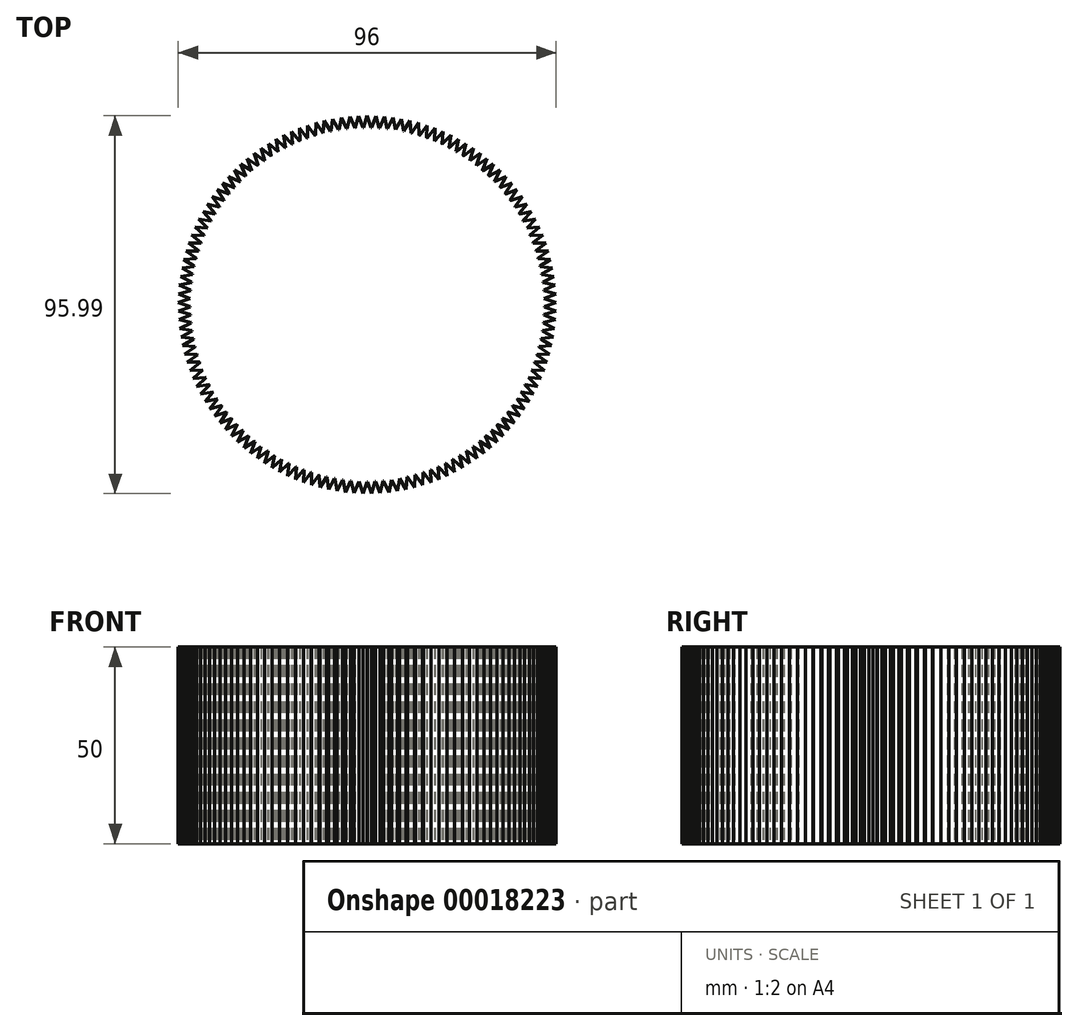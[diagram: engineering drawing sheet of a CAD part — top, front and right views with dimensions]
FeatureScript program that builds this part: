
annotation { "Feature Type Name" : "Feature", "Feature Type Description" : "" }
export const myFeature = defineFeature(function(context is Context, id is Id, definition is map)
    precondition{}
    {
        {
            var Q0;
            Q0=qCreatedBy(makeId("Top.planeOp"),FACE);
            var sketch = newSketch(context, id + "F0", { "sketchPlane" : qUnion([Q0])});
            skCircle(sketch, "E0", {"center": v(0, 0) * mm, "radius": 46.5 * mm, "construction": true});
            skLineSegment(sketch, "E1", {"start": v(0, 0) * mm, "end": v(0, 46.5) * mm, "construction": true});
            skCircle(sketch, "E2.0", {"center": v(0, 0) * mm, "radius": 48 * mm, "construction": true});
            skCircle(sketch, "E3.0", {"center": v(0, 0) * mm, "radius": 45 * mm});
            skLineSegment(sketch, "E4", {"start": v(-0.98, 44.99) * mm, "end": v(0, 48) * mm});
            skLineSegment(sketch, "E5", {"start": v(0, 48) * mm, "end": v(0.98, 44.99) * mm});
            skLineSegment(sketch, "E6.1.0", {"start": v(-2.2, 47.95) * mm, "end": v(-1.09, 44.99) * mm});
            skLineSegment(sketch, "E6.1.1", {"start": v(-3.04, 44.9) * mm, "end": v(-2.2, 47.95) * mm});
            skLineSegment(sketch, "E6.2.0", {"start": v(-4.4, 47.8) * mm, "end": v(-3.15, 44.89) * mm});
            skLineSegment(sketch, "E6.2.1", {"start": v(-5.1, 44.71) * mm, "end": v(-4.4, 47.8) * mm});
            skLineSegment(sketch, "E6.3.0", {"start": v(-6.58, 47.55) * mm, "end": v(-5.2, 44.7) * mm});
            skLineSegment(sketch, "E6.3.1", {"start": v(-7.14, 44.43) * mm, "end": v(-6.58, 47.55) * mm});
            skLineSegment(sketch, "E6.4.0", {"start": v(-8.76, 47.2) * mm, "end": v(-7.25, 44.41) * mm});
            skLineSegment(sketch, "E6.4.1", {"start": v(-9.17, 44.06) * mm, "end": v(-8.76, 47.2) * mm});
            skLineSegment(sketch, "E6.5.0", {"start": v(-10.91, 46.74) * mm, "end": v(-9.27, 44.03) * mm});
            skLineSegment(sketch, "E6.5.1", {"start": v(-11.18, 43.59) * mm, "end": v(-10.91, 46.74) * mm});
            skLineSegment(sketch, "E6.6.0", {"start": v(-13.04, 46.2) * mm, "end": v(-11.28, 43.56) * mm});
            skLineSegment(sketch, "E6.6.1", {"start": v(-13.17, 43.03) * mm, "end": v(-13.04, 46.2) * mm});
            skLineSegment(sketch, "E6.7.0", {"start": v(-15.15, 45.55) * mm, "end": v(-13.27, 43) * mm});
            skLineSegment(sketch, "E6.7.1", {"start": v(-15.12, 42.38) * mm, "end": v(-15.15, 45.55) * mm});
            skLineSegment(sketch, "E6.8.0", {"start": v(-17.22, 44.8) * mm, "end": v(-15.23, 42.35) * mm});
            skLineSegment(sketch, "E6.8.1", {"start": v(-17.05, 41.64) * mm, "end": v(-17.22, 44.8) * mm});
            skLineSegment(sketch, "E6.9.0", {"start": v(-19.25, 43.97) * mm, "end": v(-17.15, 41.6) * mm});
            skLineSegment(sketch, "E6.9.1", {"start": v(-18.94, 40.82) * mm, "end": v(-19.25, 43.97) * mm});
            skLineSegment(sketch, "E6.10.0", {"start": v(-21.25, 43.04) * mm, "end": v(-19.04, 40.77) * mm});
            skLineSegment(sketch, "E6.10.1", {"start": v(-20.8, 39.9) * mm, "end": v(-21.25, 43.04) * mm});
            skLineSegment(sketch, "E6.11.0", {"start": v(-23.2, 42.02) * mm, "end": v(-20.89, 39.86) * mm});
            skLineSegment(sketch, "E6.11.1", {"start": v(-22.6, 38.91) * mm, "end": v(-23.2, 42.02) * mm});
            skLineSegment(sketch, "E6.12.0", {"start": v(-25.1, 40.91) * mm, "end": v(-22.7, 38.86) * mm});
            skLineSegment(sketch, "E6.12.1", {"start": v(-24.36, 37.83) * mm, "end": v(-25.1, 40.91) * mm});
            skLineSegment(sketch, "E6.13.0", {"start": v(-26.95, 39.72) * mm, "end": v(-24.45, 37.78) * mm});
            skLineSegment(sketch, "E6.13.1", {"start": v(-26.07, 36.68) * mm, "end": v(-26.95, 39.72) * mm});
            skLineSegment(sketch, "E6.14.0", {"start": v(-28.75, 38.44) * mm, "end": v(-26.16, 36.62) * mm});
            skLineSegment(sketch, "E6.14.1", {"start": v(-27.73, 35.44) * mm, "end": v(-28.75, 38.44) * mm});
            skLineSegment(sketch, "E6.15.0", {"start": v(-30.48, 37.08) * mm, "end": v(-27.81, 35.38) * mm});
            skLineSegment(sketch, "E6.15.1", {"start": v(-29.32, 34.14) * mm, "end": v(-30.48, 37.08) * mm});
            skLineSegment(sketch, "E6.16.0", {"start": v(-32.15, 35.65) * mm, "end": v(-29.4, 34.07) * mm});
            skLineSegment(sketch, "E6.16.1", {"start": v(-30.86, 32.76) * mm, "end": v(-32.15, 35.65) * mm});
            skLineSegment(sketch, "E6.17.0", {"start": v(-33.75, 34.14) * mm, "end": v(-30.93, 32.68) * mm});
            skLineSegment(sketch, "E6.17.1", {"start": v(-32.33, 31.3) * mm, "end": v(-33.75, 34.14) * mm});
            skLineSegment(sketch, "E6.18.0", {"start": v(-35.28, 32.55) * mm, "end": v(-32.4, 31.23) * mm});
            skLineSegment(sketch, "E6.18.1", {"start": v(-33.73, 29.8) * mm, "end": v(-35.28, 32.55) * mm});
            skLineSegment(sketch, "E6.19.0", {"start": v(-36.73, 30.9) * mm, "end": v(-33.8, 29.71) * mm});
            skLineSegment(sketch, "E6.19.1", {"start": v(-35.06, 28.21) * mm, "end": v(-36.73, 30.9) * mm});
            skLineSegment(sketch, "E6.20.0", {"start": v(-38.1, 29.18) * mm, "end": v(-35.12, 28.13) * mm});
            skLineSegment(sketch, "E6.20.1", {"start": v(-36.31, 26.58) * mm, "end": v(-38.1, 29.18) * mm});
            skLineSegment(sketch, "E6.21.0", {"start": v(-39.4, 27.4) * mm, "end": v(-36.38, 26.5) * mm});
            skLineSegment(sketch, "E6.21.1", {"start": v(-37.5, 24.88) * mm, "end": v(-39.4, 27.4) * mm});
            skLineSegment(sketch, "E6.22.0", {"start": v(-40.62, 25.57) * mm, "end": v(-37.55, 24.8) * mm});
            skLineSegment(sketch, "E6.22.1", {"start": v(-38.6, 23.14) * mm, "end": v(-40.62, 25.57) * mm});
            skLineSegment(sketch, "E6.23.0", {"start": v(-41.75, 23.68) * mm, "end": v(-38.65, 23.05) * mm});
            skLineSegment(sketch, "E6.23.1", {"start": v(-39.62, 21.35) * mm, "end": v(-41.75, 23.68) * mm});
            skLineSegment(sketch, "E6.24.0", {"start": v(-42.8, 21.74) * mm, "end": v(-39.67, 21.25) * mm});
            skLineSegment(sketch, "E6.24.1", {"start": v(-40.55, 19.5) * mm, "end": v(-42.8, 21.74) * mm});
            skLineSegment(sketch, "E6.25.0", {"start": v(-43.75, 19.76) * mm, "end": v(-40.6, 19.4) * mm});
            skLineSegment(sketch, "E6.25.1", {"start": v(-41.4, 17.63) * mm, "end": v(-43.75, 19.76) * mm});
            skLineSegment(sketch, "E6.26.0", {"start": v(-44.6, 17.73) * mm, "end": v(-41.45, 17.53) * mm});
            skLineSegment(sketch, "E6.26.1", {"start": v(-42.17, 15.71) * mm, "end": v(-44.6, 17.73) * mm});
            skLineSegment(sketch, "E6.27.0", {"start": v(-45.37, 15.67) * mm, "end": v(-42.2, 15.6) * mm});
            skLineSegment(sketch, "E6.27.1", {"start": v(-42.84, 13.76) * mm, "end": v(-45.37, 15.67) * mm});
            skLineSegment(sketch, "E6.28.0", {"start": v(-46.04, 13.57) * mm, "end": v(-42.88, 13.66) * mm});
            skLineSegment(sketch, "E6.28.1", {"start": v(-43.43, 11.78) * mm, "end": v(-46.04, 13.57) * mm});
            skLineSegment(sketch, "E6.29.0", {"start": v(-46.62, 11.45) * mm, "end": v(-43.46, 11.68) * mm});
            skLineSegment(sketch, "E6.29.1", {"start": v(-43.92, 9.78) * mm, "end": v(-46.62, 11.45) * mm});
            skLineSegment(sketch, "E6.30.0", {"start": v(-47.1, 9.3) * mm, "end": v(-43.95, 9.67) * mm});
            skLineSegment(sketch, "E6.30.1", {"start": v(-44.33, 7.75) * mm, "end": v(-47.1, 9.3) * mm});
            skLineSegment(sketch, "E6.31.0", {"start": v(-47.47, 7.13) * mm, "end": v(-44.35, 7.65) * mm});
            skLineSegment(sketch, "E6.31.1", {"start": v(-44.64, 5.71) * mm, "end": v(-47.47, 7.13) * mm});
            skLineSegment(sketch, "E6.32.0", {"start": v(-47.74, 4.94) * mm, "end": v(-44.65, 5.6) * mm});
            skLineSegment(sketch, "E6.32.1", {"start": v(-44.85, 3.66) * mm, "end": v(-47.74, 4.94) * mm});
            skLineSegment(sketch, "E6.33.0", {"start": v(-47.92, 2.75) * mm, "end": v(-44.86, 3.55) * mm});
            skLineSegment(sketch, "E6.33.1", {"start": v(-44.97, 1.6) * mm, "end": v(-47.92, 2.75) * mm});
            skLineSegment(sketch, "E6.34.0", {"start": v(-48, 0.55) * mm, "end": v(-44.98, 1.5) * mm});
            skLineSegment(sketch, "E6.34.1", {"start": v(-45, -0.46) * mm, "end": v(-48, 0.55) * mm});
            skLineSegment(sketch, "E6.35.0", {"start": v(-47.97, -1.65) * mm, "end": v(-45, -0.57) * mm});
            skLineSegment(sketch, "E6.35.1", {"start": v(-44.93, -2.52) * mm, "end": v(-47.97, -1.65) * mm});
            skLineSegment(sketch, "E6.36.0", {"start": v(-47.85, -3.85) * mm, "end": v(-44.92, -2.63) * mm});
            skLineSegment(sketch, "E6.36.1", {"start": v(-44.77, -4.58) * mm, "end": v(-47.85, -3.85) * mm});
            skLineSegment(sketch, "E6.37.0", {"start": v(-47.62, -6.04) * mm, "end": v(-44.76, -4.69) * mm});
            skLineSegment(sketch, "E6.37.1", {"start": v(-44.5, -6.63) * mm, "end": v(-47.62, -6.04) * mm});
            skLineSegment(sketch, "E6.38.0", {"start": v(-47.3, -8.21) * mm, "end": v(-44.5, -6.74) * mm});
            skLineSegment(sketch, "E6.38.1", {"start": v(-44.16, -8.66) * mm, "end": v(-47.3, -8.21) * mm});
            skLineSegment(sketch, "E6.39.0", {"start": v(-46.87, -10.37) * mm, "end": v(-44.14, -8.77) * mm});
            skLineSegment(sketch, "E6.39.1", {"start": v(-43.71, -10.68) * mm, "end": v(-46.87, -10.37) * mm});
            skLineSegment(sketch, "E6.40.0", {"start": v(-46.34, -12.51) * mm, "end": v(-43.69, -10.78) * mm});
            skLineSegment(sketch, "E6.40.1", {"start": v(-43.18, -12.67) * mm, "end": v(-46.34, -12.51) * mm});
            skLineSegment(sketch, "E6.41.0", {"start": v(-45.72, -14.62) * mm, "end": v(-43.15, -12.77) * mm});
            skLineSegment(sketch, "E6.41.1", {"start": v(-42.55, -14.64) * mm, "end": v(-45.72, -14.62) * mm});
            skLineSegment(sketch, "E6.42.0", {"start": v(-45, -16.7) * mm, "end": v(-42.52, -14.74) * mm});
            skLineSegment(sketch, "E6.42.1", {"start": v(-41.84, -16.57) * mm, "end": v(-45, -16.7) * mm});
            skLineSegment(sketch, "E6.43.0", {"start": v(-44.19, -18.75) * mm, "end": v(-41.8, -16.67) * mm});
            skLineSegment(sketch, "E6.43.1", {"start": v(-41.03, -18.47) * mm, "end": v(-44.19, -18.75) * mm});
            skLineSegment(sketch, "E6.44.0", {"start": v(-43.28, -20.76) * mm, "end": v(-40.99, -18.57) * mm});
            skLineSegment(sketch, "E6.44.1", {"start": v(-40.14, -20.34) * mm, "end": v(-43.28, -20.76) * mm});
            skLineSegment(sketch, "E6.45.0", {"start": v(-42.28, -22.72) * mm, "end": v(-40.1, -20.43) * mm});
            skLineSegment(sketch, "E6.45.1", {"start": v(-39.17, -22.15) * mm, "end": v(-42.28, -22.72) * mm});
            skLineSegment(sketch, "E6.46.0", {"start": v(-41.2, -24.63) * mm, "end": v(-39.12, -22.25) * mm});
            skLineSegment(sketch, "E6.46.1", {"start": v(-38.11, -23.93) * mm, "end": v(-41.2, -24.63) * mm});
            skLineSegment(sketch, "E6.47.0", {"start": v(-40.02, -26.5) * mm, "end": v(-38.05, -24.02) * mm});
            skLineSegment(sketch, "E6.47.1", {"start": v(-36.97, -25.65) * mm, "end": v(-40.02, -26.5) * mm});
            skLineSegment(sketch, "E6.48.0", {"start": v(-38.77, -28.3) * mm, "end": v(-36.91, -25.74) * mm});
            skLineSegment(sketch, "E6.48.1", {"start": v(-35.76, -27.32) * mm, "end": v(-38.77, -28.3) * mm});
            skLineSegment(sketch, "E7.2.49.0", {"start": v(-37.43, -30.05) * mm, "end": v(-35.7, -27.4) * mm});
            skLineSegment(sketch, "E7.3.49.0", {"start": v(-34.47, -28.93) * mm, "end": v(-37.43, -30.05) * mm});
            skLineSegment(sketch, "E7.2.50.0", {"start": v(-36.01, -31.73) * mm, "end": v(-34.4, -29.01) * mm});
            skLineSegment(sketch, "E7.3.50.0", {"start": v(-33.1, -30.48) * mm, "end": v(-36.01, -31.73) * mm});
            skLineSegment(sketch, "E7.2.51.0", {"start": v(-34.52, -33.35) * mm, "end": v(-33.03, -30.56) * mm});
            skLineSegment(sketch, "E7.3.51.0", {"start": v(-31.67, -31.96) * mm, "end": v(-34.52, -33.35) * mm});
            skLineSegment(sketch, "E7.2.52.0", {"start": v(-32.95, -34.9) * mm, "end": v(-31.6, -32.04) * mm});
            skLineSegment(sketch, "E7.3.52.0", {"start": v(-30.18, -33.38) * mm, "end": v(-32.95, -34.9) * mm});
            skLineSegment(sketch, "E7.2.53.0", {"start": v(-31.32, -36.37) * mm, "end": v(-30.1, -33.45) * mm});
            skLineSegment(sketch, "E7.3.53.0", {"start": v(-28.61, -34.73) * mm, "end": v(-31.32, -36.37) * mm});
            skLineSegment(sketch, "E7.2.54.0", {"start": v(-29.62, -37.77) * mm, "end": v(-28.53, -34.8) * mm});
            skLineSegment(sketch, "E7.3.54.0", {"start": v(-27, -36) * mm, "end": v(-29.62, -37.77) * mm});
            skLineSegment(sketch, "E7.2.55.0", {"start": v(-27.86, -39.09) * mm, "end": v(-26.9, -36.07) * mm});
            skLineSegment(sketch, "E7.3.55.0", {"start": v(-25.31, -37.2) * mm, "end": v(-27.86, -39.09) * mm});
            skLineSegment(sketch, "E7.2.56.0", {"start": v(-26.03, -40.33) * mm, "end": v(-25.22, -37.27) * mm});
            skLineSegment(sketch, "E7.3.56.0", {"start": v(-23.58, -38.33) * mm, "end": v(-26.03, -40.33) * mm});
            skLineSegment(sketch, "E7.2.57.0", {"start": v(-24.16, -41.48) * mm, "end": v(-23.49, -38.38) * mm});
            skLineSegment(sketch, "E7.3.57.0", {"start": v(-21.8, -39.37) * mm, "end": v(-24.16, -41.48) * mm});
            skLineSegment(sketch, "E7.2.58.0", {"start": v(-22.23, -42.54) * mm, "end": v(-21.7, -39.42) * mm});
            skLineSegment(sketch, "E7.3.58.0", {"start": v(-19.97, -40.33) * mm, "end": v(-22.23, -42.54) * mm});
            skLineSegment(sketch, "E8.2.59.0", {"start": v(-20.26, -43.52) * mm, "end": v(-19.87, -40.37) * mm});
            skLineSegment(sketch, "E8.3.59.0", {"start": v(-18.1, -41.2) * mm, "end": v(-20.26, -43.52) * mm});
            skLineSegment(sketch, "E9.2.60.0", {"start": v(-18.24, -44.4) * mm, "end": v(-18, -41.24) * mm});
            skLineSegment(sketch, "E9.3.60.0", {"start": v(-16.2, -41.99) * mm, "end": v(-18.24, -44.4) * mm});
            skLineSegment(sketch, "E9.2.61.0", {"start": v(-16.19, -45.19) * mm, "end": v(-16.1, -42.02) * mm});
            skLineSegment(sketch, "E9.3.61.0", {"start": v(-14.25, -42.68) * mm, "end": v(-16.19, -45.19) * mm});
            skLineSegment(sketch, "E10.2.62.0", {"start": v(-14.1, -45.88) * mm, "end": v(-14.15, -42.72) * mm});
            skLineSegment(sketch, "E10.3.62.0", {"start": v(-12.28, -43.3) * mm, "end": v(-14.1, -45.88) * mm});
            skLineSegment(sketch, "E11.2.63.0", {"start": v(-11.98, -46.48) * mm, "end": v(-12.18, -43.32) * mm});
            skLineSegment(sketch, "E11.3.63.0", {"start": v(-10.28, -43.8) * mm, "end": v(-11.98, -46.48) * mm});
            skLineSegment(sketch, "E12.2.64.0", {"start": v(-9.84, -46.98) * mm, "end": v(-10.18, -43.83) * mm});
            skLineSegment(sketch, "E12.3.64.0", {"start": v(-8.26, -44.24) * mm, "end": v(-9.84, -46.98) * mm});
            skLineSegment(sketch, "E13.2.65.0", {"start": v(-7.67, -47.38) * mm, "end": v(-8.16, -44.25) * mm});
            skLineSegment(sketch, "E13.3.65.0", {"start": v(-6.23, -44.57) * mm, "end": v(-7.67, -47.38) * mm});
            skLineSegment(sketch, "E13.2.66.0", {"start": v(-5.5, -47.68) * mm, "end": v(-6.12, -44.58) * mm});
            skLineSegment(sketch, "E13.3.66.0", {"start": v(-4.18, -44.8) * mm, "end": v(-5.5, -47.68) * mm});
            skLineSegment(sketch, "E13.2.67.0", {"start": v(-3.3, -47.89) * mm, "end": v(-4.07, -44.82) * mm});
            skLineSegment(sketch, "E13.3.67.0", {"start": v(-2.12, -44.95) * mm, "end": v(-3.3, -47.89) * mm});
            skLineSegment(sketch, "E13.2.68.0", {"start": v(-1.1, -47.99) * mm, "end": v(-2, -44.96) * mm});
            skLineSegment(sketch, "E13.3.68.0", {"start": v(-0.05, -45) * mm, "end": v(-1.1, -47.99) * mm});
            skLineSegment(sketch, "E13.2.69.0", {"start": v(1.1, -47.99) * mm, "end": v(0.05, -45) * mm});
            skLineSegment(sketch, "E13.3.69.0", {"start": v(2, -44.96) * mm, "end": v(1.1, -47.99) * mm});
            skLineSegment(sketch, "E13.2.70.0", {"start": v(3.3, -47.89) * mm, "end": v(2.12, -44.95) * mm});
            skLineSegment(sketch, "E13.3.70.0", {"start": v(4.07, -44.82) * mm, "end": v(3.3, -47.89) * mm});
            skLineSegment(sketch, "E13.2.71.0", {"start": v(5.5, -47.68) * mm, "end": v(4.18, -44.8) * mm});
            skLineSegment(sketch, "E13.3.71.0", {"start": v(6.12, -44.58) * mm, "end": v(5.5, -47.68) * mm});
            skLineSegment(sketch, "E13.2.72.0", {"start": v(7.67, -47.38) * mm, "end": v(6.23, -44.57) * mm});
            skLineSegment(sketch, "E13.3.72.0", {"start": v(8.16, -44.25) * mm, "end": v(7.67, -47.38) * mm});
            skLineSegment(sketch, "E13.2.73.0", {"start": v(9.84, -46.98) * mm, "end": v(8.26, -44.24) * mm});
            skLineSegment(sketch, "E13.3.73.0", {"start": v(10.18, -43.83) * mm, "end": v(9.84, -46.98) * mm});
            skLineSegment(sketch, "E13.2.74.0", {"start": v(11.98, -46.48) * mm, "end": v(10.28, -43.8) * mm});
            skLineSegment(sketch, "E13.3.74.0", {"start": v(12.18, -43.32) * mm, "end": v(11.98, -46.48) * mm});
            skLineSegment(sketch, "E14.2.75.0", {"start": v(14.1, -45.88) * mm, "end": v(12.28, -43.3) * mm});
            skLineSegment(sketch, "E14.3.75.0", {"start": v(14.15, -42.72) * mm, "end": v(14.1, -45.88) * mm});
            skLineSegment(sketch, "E14.2.76.0", {"start": v(16.19, -45.19) * mm, "end": v(14.25, -42.68) * mm});
            skLineSegment(sketch, "E14.3.76.0", {"start": v(16.1, -42.02) * mm, "end": v(16.19, -45.19) * mm});
            skLineSegment(sketch, "E14.2.77.0", {"start": v(18.24, -44.4) * mm, "end": v(16.2, -41.99) * mm});
            skLineSegment(sketch, "E14.3.77.0", {"start": v(18, -41.24) * mm, "end": v(18.24, -44.4) * mm});
            skLineSegment(sketch, "E14.2.78.0", {"start": v(20.26, -43.52) * mm, "end": v(18.1, -41.2) * mm});
            skLineSegment(sketch, "E14.3.78.0", {"start": v(19.87, -40.37) * mm, "end": v(20.26, -43.52) * mm});
            skLineSegment(sketch, "E14.2.79.0", {"start": v(22.23, -42.54) * mm, "end": v(19.97, -40.33) * mm});
            skLineSegment(sketch, "E14.3.79.0", {"start": v(21.7, -39.42) * mm, "end": v(22.23, -42.54) * mm});
            skLineSegment(sketch, "E15.2.80.0", {"start": v(24.16, -41.48) * mm, "end": v(21.8, -39.37) * mm});
            skLineSegment(sketch, "E15.3.80.0", {"start": v(23.49, -38.38) * mm, "end": v(24.16, -41.48) * mm});
            skLineSegment(sketch, "E16.2.81.0", {"start": v(26.03, -40.33) * mm, "end": v(23.58, -38.33) * mm});
            skLineSegment(sketch, "E16.3.81.0", {"start": v(25.22, -37.27) * mm, "end": v(26.03, -40.33) * mm});
            skLineSegment(sketch, "E16.2.82.0", {"start": v(27.86, -39.09) * mm, "end": v(25.31, -37.2) * mm});
            skLineSegment(sketch, "E16.3.82.0", {"start": v(26.9, -36.07) * mm, "end": v(27.86, -39.09) * mm});
            skLineSegment(sketch, "E16.2.83.0", {"start": v(29.62, -37.77) * mm, "end": v(27, -36) * mm});
            skLineSegment(sketch, "E16.3.83.0", {"start": v(28.53, -34.8) * mm, "end": v(29.62, -37.77) * mm});
            skLineSegment(sketch, "E16.2.84.0", {"start": v(31.32, -36.37) * mm, "end": v(28.61, -34.73) * mm});
            skLineSegment(sketch, "E16.3.84.0", {"start": v(30.1, -33.45) * mm, "end": v(31.32, -36.37) * mm});
            skLineSegment(sketch, "E16.2.85.0", {"start": v(32.95, -34.9) * mm, "end": v(30.18, -33.38) * mm});
            skLineSegment(sketch, "E16.3.85.0", {"start": v(31.6, -32.04) * mm, "end": v(32.95, -34.9) * mm});
            skLineSegment(sketch, "E16.2.86.0", {"start": v(34.52, -33.35) * mm, "end": v(31.67, -31.96) * mm});
            skLineSegment(sketch, "E16.3.86.0", {"start": v(33.03, -30.56) * mm, "end": v(34.52, -33.35) * mm});
            skLineSegment(sketch, "E16.2.87.0", {"start": v(36.01, -31.73) * mm, "end": v(33.1, -30.48) * mm});
            skLineSegment(sketch, "E16.3.87.0", {"start": v(34.4, -29.01) * mm, "end": v(36.01, -31.73) * mm});
            skLineSegment(sketch, "E16.2.88.0", {"start": v(37.43, -30.05) * mm, "end": v(34.47, -28.93) * mm});
            skLineSegment(sketch, "E16.3.88.0", {"start": v(35.7, -27.4) * mm, "end": v(37.43, -30.05) * mm});
            skLineSegment(sketch, "E16.2.89.0", {"start": v(38.77, -28.3) * mm, "end": v(35.76, -27.32) * mm});
            skLineSegment(sketch, "E16.3.89.0", {"start": v(36.91, -25.74) * mm, "end": v(38.77, -28.3) * mm});
            skLineSegment(sketch, "E16.2.90.0", {"start": v(40.02, -26.5) * mm, "end": v(36.97, -25.65) * mm});
            skLineSegment(sketch, "E16.3.90.0", {"start": v(38.05, -24.02) * mm, "end": v(40.02, -26.5) * mm});
            skLineSegment(sketch, "E16.2.91.0", {"start": v(41.2, -24.63) * mm, "end": v(38.11, -23.93) * mm});
            skLineSegment(sketch, "E16.3.91.0", {"start": v(39.12, -22.25) * mm, "end": v(41.2, -24.63) * mm});
            skLineSegment(sketch, "E16.2.92.0", {"start": v(42.28, -22.72) * mm, "end": v(39.17, -22.15) * mm});
            skLineSegment(sketch, "E16.3.92.0", {"start": v(40.1, -20.43) * mm, "end": v(42.28, -22.72) * mm});
            skLineSegment(sketch, "E16.2.93.0", {"start": v(43.28, -20.76) * mm, "end": v(40.14, -20.34) * mm});
            skLineSegment(sketch, "E16.3.93.0", {"start": v(40.99, -18.57) * mm, "end": v(43.28, -20.76) * mm});
            skLineSegment(sketch, "E16.2.94.0", {"start": v(44.19, -18.75) * mm, "end": v(41.03, -18.47) * mm});
            skLineSegment(sketch, "E16.3.94.0", {"start": v(41.8, -16.67) * mm, "end": v(44.19, -18.75) * mm});
            skLineSegment(sketch, "E17.2.95.0", {"start": v(45, -16.7) * mm, "end": v(41.84, -16.57) * mm});
            skLineSegment(sketch, "E17.3.95.0", {"start": v(42.52, -14.74) * mm, "end": v(45, -16.7) * mm});
            skLineSegment(sketch, "E18.2.96.0", {"start": v(45.72, -14.62) * mm, "end": v(42.55, -14.64) * mm});
            skLineSegment(sketch, "E18.3.96.0", {"start": v(43.15, -12.77) * mm, "end": v(45.72, -14.62) * mm});
            skLineSegment(sketch, "E18.2.97.0", {"start": v(46.34, -12.51) * mm, "end": v(43.18, -12.67) * mm});
            skLineSegment(sketch, "E18.3.97.0", {"start": v(43.69, -10.78) * mm, "end": v(46.34, -12.51) * mm});
            skLineSegment(sketch, "E18.2.98.0", {"start": v(46.87, -10.37) * mm, "end": v(43.71, -10.68) * mm});
            skLineSegment(sketch, "E18.3.98.0", {"start": v(44.14, -8.77) * mm, "end": v(46.87, -10.37) * mm});
            skLineSegment(sketch, "E18.2.99.0", {"start": v(47.3, -8.21) * mm, "end": v(44.16, -8.66) * mm});
            skLineSegment(sketch, "E18.3.99.0", {"start": v(44.5, -6.74) * mm, "end": v(47.3, -8.21) * mm});
            skLineSegment(sketch, "E18.2.100.0", {"start": v(47.62, -6.04) * mm, "end": v(44.5, -6.63) * mm});
            skLineSegment(sketch, "E18.3.100.0", {"start": v(44.76, -4.69) * mm, "end": v(47.62, -6.04) * mm});
            skLineSegment(sketch, "E18.2.101.0", {"start": v(47.85, -3.85) * mm, "end": v(44.77, -4.58) * mm});
            skLineSegment(sketch, "E18.3.101.0", {"start": v(44.92, -2.63) * mm, "end": v(47.85, -3.85) * mm});
            skLineSegment(sketch, "E18.2.102.0", {"start": v(47.97, -1.65) * mm, "end": v(44.93, -2.52) * mm});
            skLineSegment(sketch, "E18.3.102.0", {"start": v(45, -0.57) * mm, "end": v(47.97, -1.65) * mm});
            skLineSegment(sketch, "E18.2.103.0", {"start": v(48, 0.55) * mm, "end": v(45, -0.46) * mm});
            skLineSegment(sketch, "E18.3.103.0", {"start": v(44.98, 1.5) * mm, "end": v(48, 0.55) * mm});
            skLineSegment(sketch, "E18.2.104.0", {"start": v(47.92, 2.75) * mm, "end": v(44.97, 1.6) * mm});
            skLineSegment(sketch, "E18.3.104.0", {"start": v(44.86, 3.55) * mm, "end": v(47.92, 2.75) * mm});
            skLineSegment(sketch, "E18.2.105.0", {"start": v(47.74, 4.94) * mm, "end": v(44.85, 3.66) * mm});
            skLineSegment(sketch, "E18.3.105.0", {"start": v(44.65, 5.6) * mm, "end": v(47.74, 4.94) * mm});
            skLineSegment(sketch, "E18.2.106.0", {"start": v(47.47, 7.13) * mm, "end": v(44.64, 5.71) * mm});
            skLineSegment(sketch, "E18.3.106.0", {"start": v(44.35, 7.65) * mm, "end": v(47.47, 7.13) * mm});
            skLineSegment(sketch, "E18.2.107.0", {"start": v(47.1, 9.3) * mm, "end": v(44.33, 7.75) * mm});
            skLineSegment(sketch, "E18.3.107.0", {"start": v(43.95, 9.67) * mm, "end": v(47.1, 9.3) * mm});
            skLineSegment(sketch, "E18.2.108.0", {"start": v(46.62, 11.45) * mm, "end": v(43.92, 9.78) * mm});
            skLineSegment(sketch, "E18.3.108.0", {"start": v(43.46, 11.68) * mm, "end": v(46.62, 11.45) * mm});
            skLineSegment(sketch, "E18.2.109.0", {"start": v(46.04, 13.57) * mm, "end": v(43.43, 11.78) * mm});
            skLineSegment(sketch, "E18.3.109.0", {"start": v(42.88, 13.66) * mm, "end": v(46.04, 13.57) * mm});
            skLineSegment(sketch, "E18.2.110.0", {"start": v(45.37, 15.67) * mm, "end": v(42.84, 13.76) * mm});
            skLineSegment(sketch, "E18.3.110.0", {"start": v(42.2, 15.6) * mm, "end": v(45.37, 15.67) * mm});
            skLineSegment(sketch, "E19.2.111.0", {"start": v(44.6, 17.73) * mm, "end": v(42.17, 15.71) * mm});
            skLineSegment(sketch, "E19.3.111.0", {"start": v(41.45, 17.53) * mm, "end": v(44.6, 17.73) * mm});
            skLineSegment(sketch, "E19.2.112.0", {"start": v(43.75, 19.76) * mm, "end": v(41.4, 17.63) * mm});
            skLineSegment(sketch, "E19.3.112.0", {"start": v(40.6, 19.4) * mm, "end": v(43.75, 19.76) * mm});
            skLineSegment(sketch, "E19.2.113.0", {"start": v(42.8, 21.74) * mm, "end": v(40.55, 19.5) * mm});
            skLineSegment(sketch, "E19.3.113.0", {"start": v(39.67, 21.25) * mm, "end": v(42.8, 21.74) * mm});
            skLineSegment(sketch, "E19.2.114.0", {"start": v(41.75, 23.68) * mm, "end": v(39.62, 21.35) * mm});
            skLineSegment(sketch, "E19.3.114.0", {"start": v(38.65, 23.05) * mm, "end": v(41.75, 23.68) * mm});
            skLineSegment(sketch, "E19.2.115.0", {"start": v(40.62, 25.57) * mm, "end": v(38.6, 23.14) * mm});
            skLineSegment(sketch, "E19.3.115.0", {"start": v(37.55, 24.8) * mm, "end": v(40.62, 25.57) * mm});
            skLineSegment(sketch, "E19.2.116.0", {"start": v(39.4, 27.4) * mm, "end": v(37.5, 24.88) * mm});
            skLineSegment(sketch, "E19.3.116.0", {"start": v(36.38, 26.5) * mm, "end": v(39.4, 27.4) * mm});
            skLineSegment(sketch, "E19.2.117.0", {"start": v(38.1, 29.18) * mm, "end": v(36.31, 26.58) * mm});
            skLineSegment(sketch, "E19.3.117.0", {"start": v(35.12, 28.13) * mm, "end": v(38.1, 29.18) * mm});
            skLineSegment(sketch, "E19.2.118.0", {"start": v(36.73, 30.9) * mm, "end": v(35.06, 28.21) * mm});
            skLineSegment(sketch, "E19.3.118.0", {"start": v(33.8, 29.71) * mm, "end": v(36.73, 30.9) * mm});
            skLineSegment(sketch, "E19.2.119.0", {"start": v(35.28, 32.55) * mm, "end": v(33.73, 29.8) * mm});
            skLineSegment(sketch, "E19.3.119.0", {"start": v(32.4, 31.23) * mm, "end": v(35.28, 32.55) * mm});
            skLineSegment(sketch, "E19.2.120.0", {"start": v(33.75, 34.14) * mm, "end": v(32.33, 31.3) * mm});
            skLineSegment(sketch, "E19.3.120.0", {"start": v(30.93, 32.68) * mm, "end": v(33.75, 34.14) * mm});
            skLineSegment(sketch, "E19.2.121.0", {"start": v(32.15, 35.65) * mm, "end": v(30.86, 32.76) * mm});
            skLineSegment(sketch, "E19.3.121.0", {"start": v(29.4, 34.07) * mm, "end": v(32.15, 35.65) * mm});
            skLineSegment(sketch, "E19.2.122.0", {"start": v(30.48, 37.08) * mm, "end": v(29.32, 34.14) * mm});
            skLineSegment(sketch, "E19.3.122.0", {"start": v(27.81, 35.38) * mm, "end": v(30.48, 37.08) * mm});
            skLineSegment(sketch, "E19.2.123.0", {"start": v(28.75, 38.44) * mm, "end": v(27.73, 35.44) * mm});
            skLineSegment(sketch, "E19.3.123.0", {"start": v(26.16, 36.62) * mm, "end": v(28.75, 38.44) * mm});
            skLineSegment(sketch, "E19.2.124.0", {"start": v(26.95, 39.72) * mm, "end": v(26.07, 36.68) * mm});
            skLineSegment(sketch, "E19.3.124.0", {"start": v(24.45, 37.78) * mm, "end": v(26.95, 39.72) * mm});
            skLineSegment(sketch, "E19.2.125.0", {"start": v(25.1, 40.91) * mm, "end": v(24.36, 37.83) * mm});
            skLineSegment(sketch, "E19.3.125.0", {"start": v(22.7, 38.86) * mm, "end": v(25.1, 40.91) * mm});
            skLineSegment(sketch, "E20.2.126.0", {"start": v(23.2, 42.02) * mm, "end": v(22.6, 38.91) * mm});
            skLineSegment(sketch, "E20.3.126.0", {"start": v(20.89, 39.86) * mm, "end": v(23.2, 42.02) * mm});
            skLineSegment(sketch, "E20.2.127.0", {"start": v(21.25, 43.04) * mm, "end": v(20.8, 39.9) * mm});
            skLineSegment(sketch, "E20.3.127.0", {"start": v(19.04, 40.77) * mm, "end": v(21.25, 43.04) * mm});
            skLineSegment(sketch, "E20.2.128.0", {"start": v(19.25, 43.97) * mm, "end": v(18.94, 40.82) * mm});
            skLineSegment(sketch, "E20.3.128.0", {"start": v(17.15, 41.6) * mm, "end": v(19.25, 43.97) * mm});
            skLineSegment(sketch, "E20.2.129.0", {"start": v(17.22, 44.8) * mm, "end": v(17.05, 41.64) * mm});
            skLineSegment(sketch, "E20.3.129.0", {"start": v(15.23, 42.35) * mm, "end": v(17.22, 44.8) * mm});
            skLineSegment(sketch, "E20.2.130.0", {"start": v(15.15, 45.55) * mm, "end": v(15.12, 42.38) * mm});
            skLineSegment(sketch, "E20.3.130.0", {"start": v(13.27, 43) * mm, "end": v(15.15, 45.55) * mm});
            skLineSegment(sketch, "E20.2.131.0", {"start": v(13.04, 46.2) * mm, "end": v(13.17, 43.03) * mm});
            skLineSegment(sketch, "E20.3.131.0", {"start": v(11.28, 43.56) * mm, "end": v(13.04, 46.2) * mm});
            skLineSegment(sketch, "E20.2.132.0", {"start": v(10.91, 46.74) * mm, "end": v(11.18, 43.59) * mm});
            skLineSegment(sketch, "E20.3.132.0", {"start": v(9.27, 44.03) * mm, "end": v(10.91, 46.74) * mm});
            skLineSegment(sketch, "E20.2.133.0", {"start": v(8.76, 47.2) * mm, "end": v(9.17, 44.06) * mm});
            skLineSegment(sketch, "E20.3.133.0", {"start": v(7.25, 44.41) * mm, "end": v(8.76, 47.2) * mm});
            skLineSegment(sketch, "E20.2.134.0", {"start": v(6.58, 47.55) * mm, "end": v(7.14, 44.43) * mm});
            skLineSegment(sketch, "E20.3.134.0", {"start": v(5.2, 44.7) * mm, "end": v(6.58, 47.55) * mm});
            skLineSegment(sketch, "E21.2.135.0", {"start": v(4.4, 47.8) * mm, "end": v(5.1, 44.71) * mm});
            skLineSegment(sketch, "E21.3.135.0", {"start": v(3.15, 44.89) * mm, "end": v(4.4, 47.8) * mm});
            skLineSegment(sketch, "E21.2.136.0", {"start": v(2.2, 47.95) * mm, "end": v(3.04, 44.9) * mm});
            skLineSegment(sketch, "E21.3.136.0", {"start": v(1.09, 44.99) * mm, "end": v(2.2, 47.95) * mm});
            skSolve(sketch);
        }
        {
            var Q0;
            Q0 = qSketchRegion(id + "F0", true);
            extrude(context, id + "F1", {"entities" : qUnion([Q0]), "depth" : 50 * mm});
        }
    });
